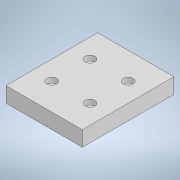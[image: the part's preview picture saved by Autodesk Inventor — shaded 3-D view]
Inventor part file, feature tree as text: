
AUTODESK INVENTOR PART (.ipt)
format: ipt  version: 2022.2 (Build 262287010, 287A)  size: 116,736 bytes
history: native  units: mm
features: sketch x2, extrude x1, hole x1
ambient origin geometry x8: Origin, YZ Plane, XZ Plane, XY Plane, X Axis, Y Axis, Z Axis, Center Point
bodies: Volumenkörper1 (feature_tree)
feature tree (4):
  extrude  "Extrusion1"  Depth=60.0mm
  hole  "Bohrung1"  [1 undecoded]
  sketch  "Skizze1"  dims[d0=50.0mm d1=60.0mm]
  sketch  "Skizze2"  dims[d2=10.0mm d3=0.0mm d4=25.0mm d5=25.0mm d6=3.4mm d7=6.0mm d8=6.5mm d9=3.4mm d10=90.0deg d11=8.0mm d12=20.594885mm]
note: 1 required parameter value undecoded (feature->parameter linkage not recoverable at this tier; creation-order binding heuristic only, values carry confidence <= 0.55)
